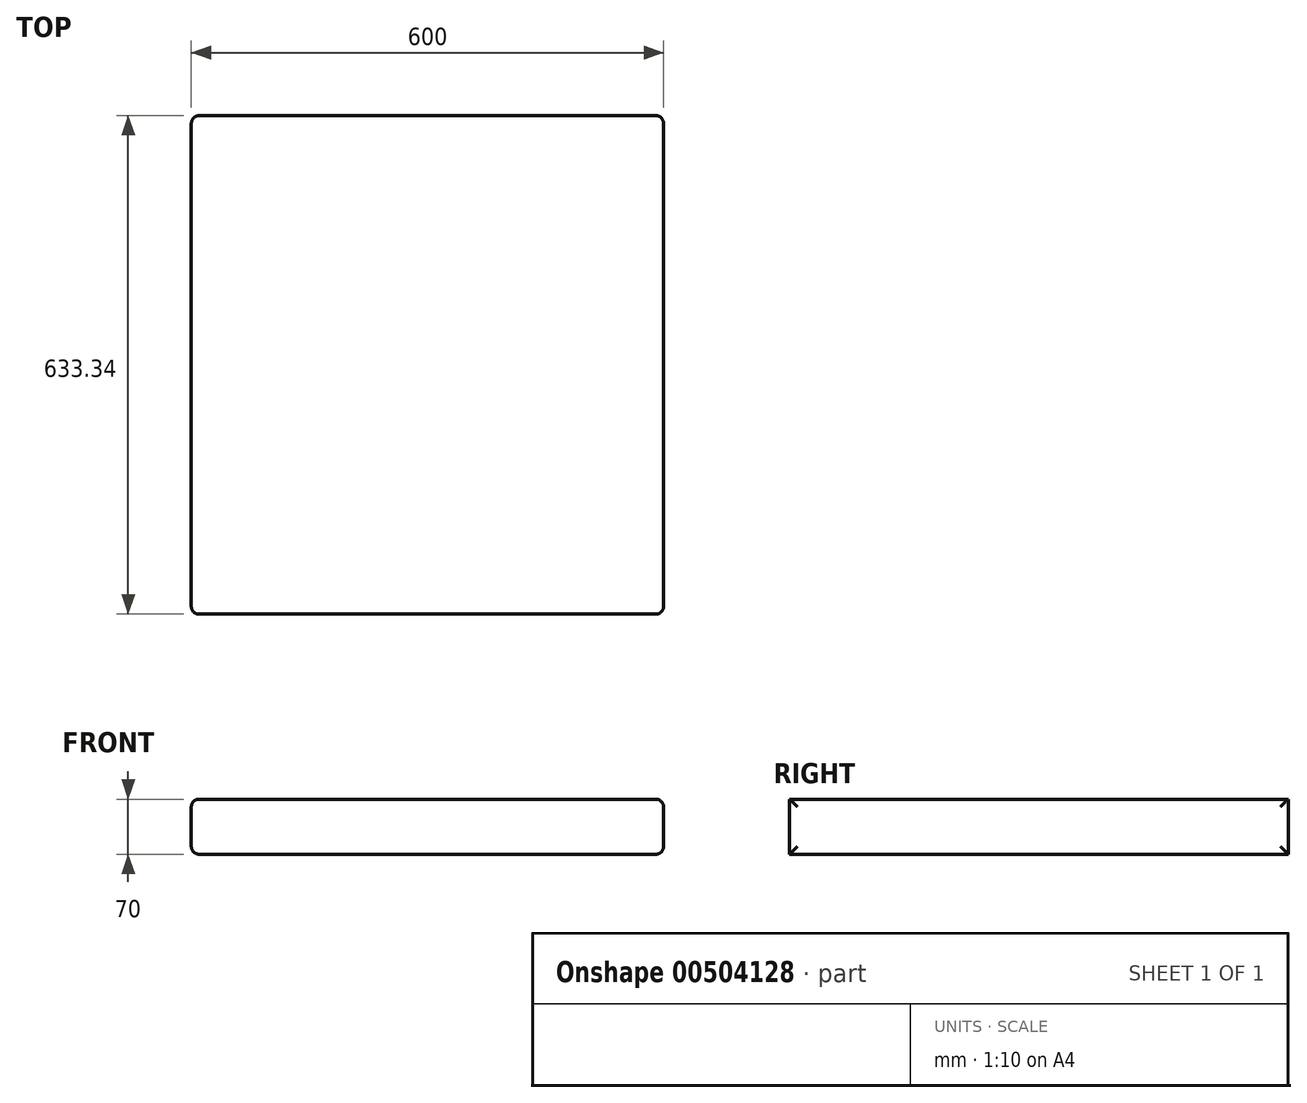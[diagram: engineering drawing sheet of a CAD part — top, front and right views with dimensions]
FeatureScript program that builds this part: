
annotation { "Feature Type Name" : "Feature", "Feature Type Description" : "" }
export const myFeature = defineFeature(function(context is Context, id is Id, definition is map)
    precondition{}
    {
        {
            var Q0;
            Q0=qCreatedBy(makeId("Top.planeOp"),FACE);
            var sketch = newSketch(context, id + "F0", { "sketchPlane" : qUnion([Q0])});
            skLineSegment(sketch, "E0.bottom", {"start": v(-300, 316.67) * mm, "end": v(300, 316.67) * mm});
            skLineSegment(sketch, "E0.top", {"start": v(-300, -316.67) * mm, "end": v(300, -316.67) * mm});
            skLineSegment(sketch, "E0.left", {"start": v(-300, 316.67) * mm, "end": v(-300, -316.67) * mm});
            skLineSegment(sketch, "E0.right", {"start": v(300, 316.67) * mm, "end": v(300, -316.67) * mm});
            skPoint(sketch, "E0.middle", {"position": v(0, 0) * mm});
            skSolve(sketch);
        }
        {
            var Q0;
            Q0=qSketchRegion(id+"F0",true);
            extrude(context, id + "F1", {"entities" : qUnion([Q0]), "depth" : 70 * mm});
        }
        {
            var Q0;
            Q0=makeQuery(id+"F1.opExtrude","SWEPT_EDGE",EDGE,{"disambiguationData":[OSD([sQuery(id+"F0.wireOp",EDGE,"E0.top"),sQuery(id+"F0.wireOp",EDGE,"E0.left")])]});
            var Q1;
            Q1=makeQuery(id+"F1.opExtrude","SWEPT_EDGE",EDGE,{"disambiguationData":[OSD([sQuery(id+"F0.wireOp",EDGE,"E0.top"),sQuery(id+"F0.wireOp",EDGE,"E0.right")])]});
            var Q2;
            Q2=makeQuery(id+"F1.opExtrude","SWEPT_EDGE",EDGE,{"disambiguationData":[OSD([sQuery(id+"F0.wireOp",EDGE,"E0.bottom"),sQuery(id+"F0.wireOp",EDGE,"E0.right")])]});
            var Q3;
            Q3=makeQuery(id+"F1.opExtrude","SWEPT_EDGE",EDGE,{"disambiguationData":[OSD([sQuery(id+"F0.wireOp",EDGE,"E0.bottom"),sQuery(id+"F0.wireOp",EDGE,"E0.left")])]});
            var Q4;
            Q4=makeQuery(id+"F1.opExtrude","CAP_EDGE",EDGE,{"disambiguationData":[OSD([sQuery(id+"F0.wireOp",EDGE,"E0.left")])],"isStart":false});
            var Q5;
            Q5=makeQuery(id+"F1.opExtrude","CAP_EDGE",EDGE,{"disambiguationData":[OSD([sQuery(id+"F0.wireOp",EDGE,"E0.right")])],"isStart":false});
            var Q6;
            Q6=makeQuery(id+"F1.opExtrude","CAP_EDGE",EDGE,{"disambiguationData":[OSD([sQuery(id+"F0.wireOp",EDGE,"E0.right")])],"isStart":true});
            var Q7;
            Q7=makeQuery(id+"F1.opExtrude","CAP_EDGE",EDGE,{"disambiguationData":[OSD([sQuery(id+"F0.wireOp",EDGE,"E0.left")])],"isStart":true});
            fillet(context, id + "F2", {"entities" : qUnion([Q0, Q1, Q2, Q3, Q4, Q5, Q6, Q7]), "radius" : 10 * mm, "tangentPropagation" : true, "allowEdgeOverflow" : false});
        }
    });
